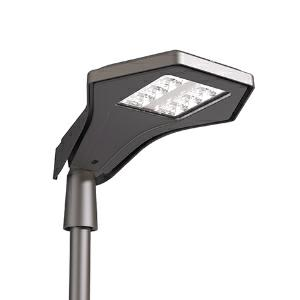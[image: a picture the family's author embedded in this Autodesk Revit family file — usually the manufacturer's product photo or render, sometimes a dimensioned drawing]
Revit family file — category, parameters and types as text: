
# Revit family: 3f_filippi_-_3f_manta_medio_3f_filippi_-_7020_-_3f_manta_an_185-730_medium
name_source: partatom
category: Lighting Fixtures
units: mm (PartAtom-declared; Revit-internal decimal feet)

## family parameters
Cut with Voids When Loaded = No
Host = Face
Light Source = No
Part Type = Normal
Room Calculation Point = No
Round Connector Dimension = Use Diameter
Shared = No

## types (1)
- 3F Filippi - 3F Manta Medio (1 x LED, 22451 lm, 195 W, 3000 K)
    Apparent Load = 195 VA
    Approval mark = CE
    CIE Flux Codes = 42 81 99 100 100
    Color Rendering = 70
    Color Temperature = 3000 K
    Control Gear = Electronic ballast
    Default Elevation = 1800 mm
    Description = ILLUMINOTECHNICAL
Luminous efficiency 100% (DLOR 100%, ULOR 0%).
Initial luminous flux of the luminaire 22451 lm.
Asymmetric distribution with medium bilateral.
BUG (Backlight, Uplight, Glare) IESNA TM-15: B3 U0 G2.
Beam angle: 141° - 70°.
Luminous efficacy 115 lm/W.
Lifetime (L93/B10): 30000 h. (tq+25°C)
Lifetime (L90/B10): 50000 h. (tq+25°C)
Lifetime (L85/B10): 80000 h. (tq+25°C)
Lifetime (L80/B10): 100000 h. (tq+25°C)
Lifetime (L90/B20): 50000 h. (tq+45°C)
Sudden decreased luminous flux after 50000 hours: 0% (C0).
Photobiological safety in compliance with IEC/TR 62778: RG0 risk exempt, (IEC 62471).
In compliance with IEC/EN 62722-2-1 - IEC/EN 62717 standards.

SOURCE
Squared LED module 185W/730.
Source with special protection against aggressive chemically-volatile substances for standard LED technology.
Energy efficiency class (UE 2019/2020 - UE 2019/2015): D.
CIE 13.3 Colour rendering index: CRI >70 (R9 <50%).
IES TM-30 Fidelity Index: Rf = 72 Rg = 95.
CCT nominal colour temperature 3000 K.
Colour initial tolerance (MacAdam): SDCM 5.

MECHANICAL
Aerodynamically-shaped die-cast aluminium double-shell body for low wind resistance (frontal: 0.0446 m²; lateral: 0.0505 m²), equipped with fins to optimize the cooling of the internal components.
Shell closure using stainless steel screws on stainless steel bushings, with hinged opening for easy access to the wiring compartment, equipped with system against accidental closure.
Polyester powder coating with degreasing pre-treatment and phosphate layer deposit on the metal, UV stabilised, corrosion resistant, anthracite colour, salt spray resistance ISO 9227 >1000 h.
Parabolic cellular optics with total recovery, entirely made of semi-specular high reflection aluminium with titanium and magnesium surface treatment, to maintain optical performance over time.
Polyurethane foam seals, ecological, anti-aging, installed using a continuous automatic process with no joints.
VT extra transparent tempered glass diffuser, 4 mm thick, non-combustible, with Heat Soak Test (HST) thermal treatment, which drastically reduces the risk of spontaneous breakage.
Stainless steel internal and external screws.
Luminaire with limited surface temperature. - D - (EN 60598-2-24)
Dimensions: 660x440 mm, height 166 mm. Weight 11.115 kg.
IP66 protection degree.
Mechanical strength to impacts IK08 (5 joule).
Glow-wire test resistance 960°C.

ELECTRICAL
Halogen Free electronic wiring 230V-50/60Hz, power factor 0.97, THD <25%, constant output current, class I, 1 driver.
Power of the luminaire 195 W.
ENEC - CE.
SAFE FLICKER: PstLM=<1 and SVM=<0.4 (IEC TR 61547-1 and IEC TR 63158), to ensure a more comfortable and safe light.
Ambient temperature from -20°C to +45°C.
Temperature class T6 max 85°C.
Safety break switch to shut off the power supply when opening the device.
Insulation voltage 6kV via Sourge Protector.
SPD type 2+3 (combined) device to protect against voltage surges up to 10 kV in common and differential mode.
Thermal protection of the LED module via NTC sensor (Negative Temperature Coefficient).
M20x1.5 IP68 nylon cable gland for feeding input (cables with an min-max diameter 6-13mm).
Pressure compensating valve with anti-condensation effect.
Relative humidity UR: <85%.

INSTALLATION
Post-top / arm / wall.
Installation with always necessary "Pole fixing" accessory (see accessories).
All accessories dedicated to this product are available on the Catalog and on our website www.3F-Filippi.com.

ACCESSORIES
Pole mount in die-cast aluminium with the same paint treatment as the body (for Ø 60 mm and Ø 76 mm poles) equipped with special teeth for adjusting the inclination on the head of the device by ± 20° with an adjustment pitch of 5°.
Possibility of installing on vertical pole (pole head) and horizontal pole (arm).
Mounting on the device using the supplied stainless steel screws on self-locking stainless steel nuts.
A0439 - Pole mounting diameter 60 mm.
A0440 - Pole mounting diameter 76 mm.

APPLICATIONS
Outdoor environments, general lighting, work and roadway lighting, transit areas and building perimeters, parking lots, trade fairs.
Control of light pollution, in accordance with the legislative requirements in force.

LIGHT MANAGEMENT
Upon request, the appliance can be supplied with "Virtual Midnight" programming.

WARNING
Luminaire designed for disposal/recycling at end-of-life.
Replaceable (LED only) light source by a professional. Replaceable control gear by a professional.
    Height = 166 mm
    Lamp = 1 x LED
    Lamp Light Flux = 22451 lm
    Lamp Power = 195 W
    Lamp count = 1
    Length = 660 mm
    Lifetime = 50000 h
    Luminous efficacy = 115 lm/W
    Manufacturer = 3F Filippi
    ModVariant = No
    Model = 3F Filippi - 7020 - 3F Manta AN 185-730 MEDIUM
    Mounting Place = Pole
    Mounting Type = Pole top
    Number of Poles = 1
    OnlyDefault = Yes
    Power Factor = 1
    Product Name = 3F Filippi - 3F Manta Medio
    Product group = street luminaire
    ProductGroupID = 15
    Protection Class = Protection class I
    Protection Degree = IP 66
    RLX_Detail_Level = 1
    RLX_Emergency_Light_Flux = 0 lm
    RLX_Emergency_Type = 0
    RLX_Emergency_Type_DB = No
    RlxData = <blob elided: 225289 chars, md5=ac05fa9e>
    Socket = socket
    Standby Power = 0 W
    System Light Flux = 22451 lm
    System Power = 195 W
    Type Comments = Product without accessories
    Type Image = 3ffilippi_3f_manta_medium.jpg
    URL = http://relux.com
    VarID = ---
    Voltage = 0 V
    Weight = 0.00 kg
    Width = 440 mm

## geometry (parser evidence)
native form markers: Blend x4, Sweep x14
no freeform markers — native parametric forms only
